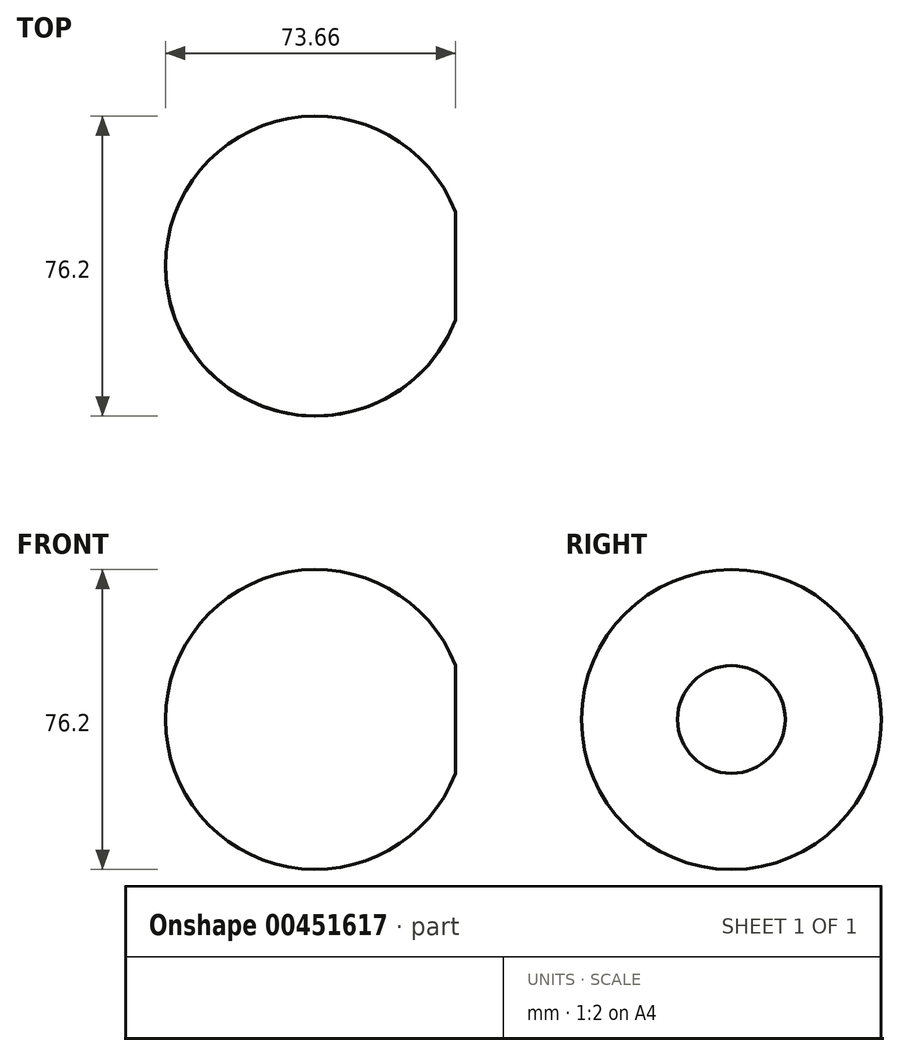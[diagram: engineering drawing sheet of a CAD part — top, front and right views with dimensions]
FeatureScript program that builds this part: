
annotation { "Feature Type Name" : "Feature", "Feature Type Description" : "" }
export const myFeature = defineFeature(function(context is Context, id is Id, definition is map)
    precondition{}
    {
        {
            var Q0;
            Q0=qCreatedBy(makeId("Top.planeOp"),FACE);
            var sketch = newSketch(context, id + "F0", { "sketchPlane" : qUnion([Q0])});
            skLineSegment(sketch, "E0", {"start": v(-38.1, 0) * mm, "end": v(38.1, 0) * mm});
            skArc(sketch, "E1", {"start": v(38.1, 0) * mm, "mid": v(0, 38.1) * mm, "end": v(-38.1, 0) * mm});
            skSolve(sketch);
        }
        {
            var Q0;
            Q0=makeQuery(id+"F0.imprint","IMPRINT",FACE,{"disambiguationData":[TD([[makeQuery(id+"F0.imprint","IMPRINT",EDGE,{"derivedFrom":sQuery(id+"F0.wireOp",EDGE,"E0")}),1.0]])]});
            var Q1;
            Q1=sQuery(id+"F0.wireOp",EDGE,"E0");
            revolve(context, id + "F1", {"entities" : qUnion([Q0]), "axis" : qUnion([Q1]), "revolveType" : RevolveType.FULL});
        }
        {
            var Q0;
            Q0=qCreatedBy(makeId("Right.planeOp"),FACE);
            cPlane(context, id + "F2", {"entities" : qUnion([Q0]), "cplaneType" : CPlaneType.OFFSET, "offset" : 35.56 * mm, "width" : 152.4 * mm, "height" : 152.4 * mm});
        }
        {
            var Q0;
            Q0=qCreatedBy(id+"F2.planeOp",FACE);
            var sketch = newSketch(context, id + "F3", { "sketchPlane" : qUnion([Q0])});
            skLineSegment(sketch, "E2.bottom", {"start": v(-52.25, 50.42) * mm, "end": v(55.83, 50.42) * mm});
            skLineSegment(sketch, "E2.top", {"start": v(-52.25, -51.18) * mm, "end": v(55.83, -51.18) * mm});
            skLineSegment(sketch, "E2.left", {"start": v(-52.25, 50.42) * mm, "end": v(-52.25, -51.18) * mm});
            skLineSegment(sketch, "E2.right", {"start": v(55.83, 50.42) * mm, "end": v(55.83, -51.18) * mm});
            skSolve(sketch);
        }
        {
            var Q0;
            Q0 = qSketchRegion(id + "F3", true);
            extrude(context, id + "F4", {"entities" : qUnion([Q0]), "operationType" : NewBodyOperationType.REMOVE, "depth" : 35.05 * mm});
        }
    });
